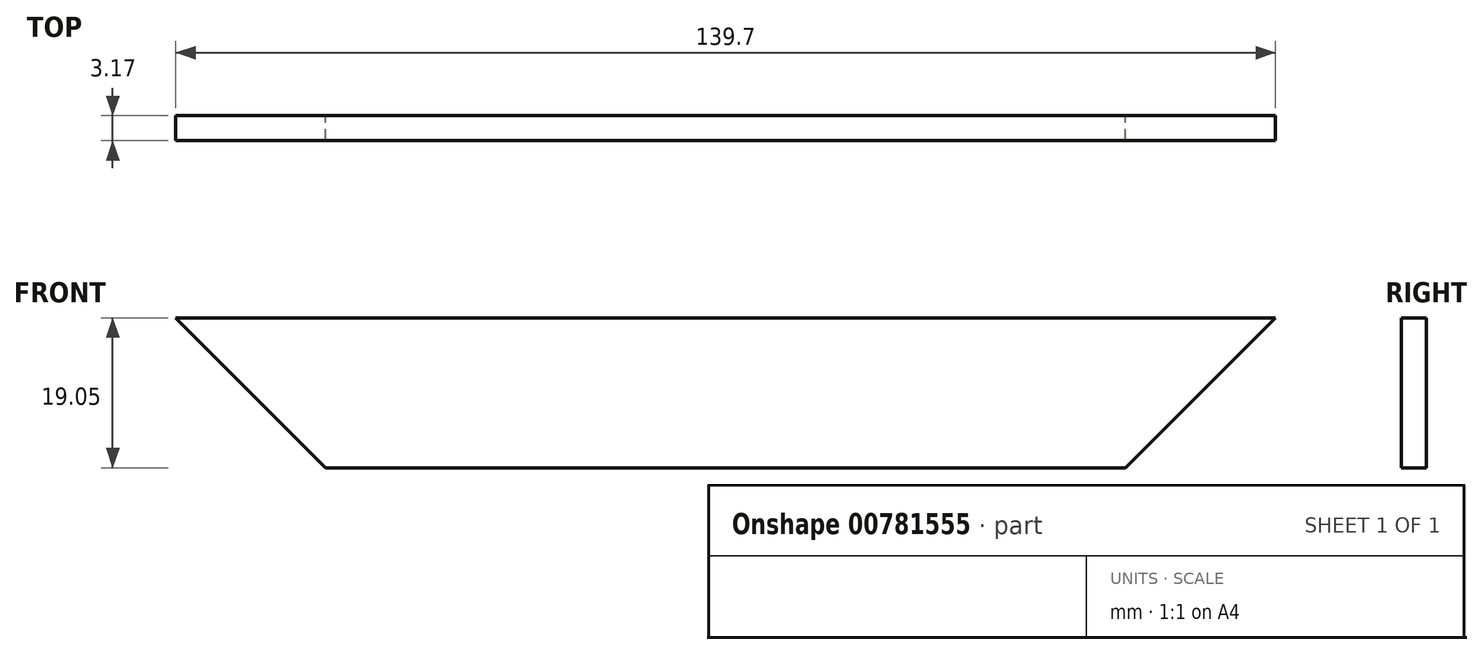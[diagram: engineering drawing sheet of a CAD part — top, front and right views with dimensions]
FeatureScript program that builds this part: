
annotation { "Feature Type Name" : "Feature", "Feature Type Description" : "" }
export const myFeature = defineFeature(function(context is Context, id is Id, definition is map)
    precondition{}
    {
        {
            var Q0;
            Q0=qCreatedBy(makeId("Front.planeOp"),FACE);
            var sketch = newSketch(context, id + "F0", { "sketchPlane" : qUnion([Q0])});
            skLineSegment(sketch, "E0.bottom", {"start": v(-66.72, 36.38) * mm, "end": v(72.98, 36.38) * mm});
            skLineSegment(sketch, "E0.top", {"start": v(-47.67, 17.33) * mm, "end": v(53.93, 17.33) * mm});
            skLineSegment(sketch, "E1", {"start": v(-66.72, 36.38) * mm, "end": v(-47.67, 17.33) * mm});
            skLineSegment(sketch, "E2", {"start": v(72.98, 36.38) * mm, "end": v(53.93, 17.33) * mm});
            skSolve(sketch);
        }
        {
            var Q0;
            Q0 = qSketchRegion(id + "F0", true);
            extrude(context, id + "F1", {"entities" : qUnion([Q0]), "depth" : 3.17 * mm, "offsetDistance" : 25.4 * mm});
        }
    });
